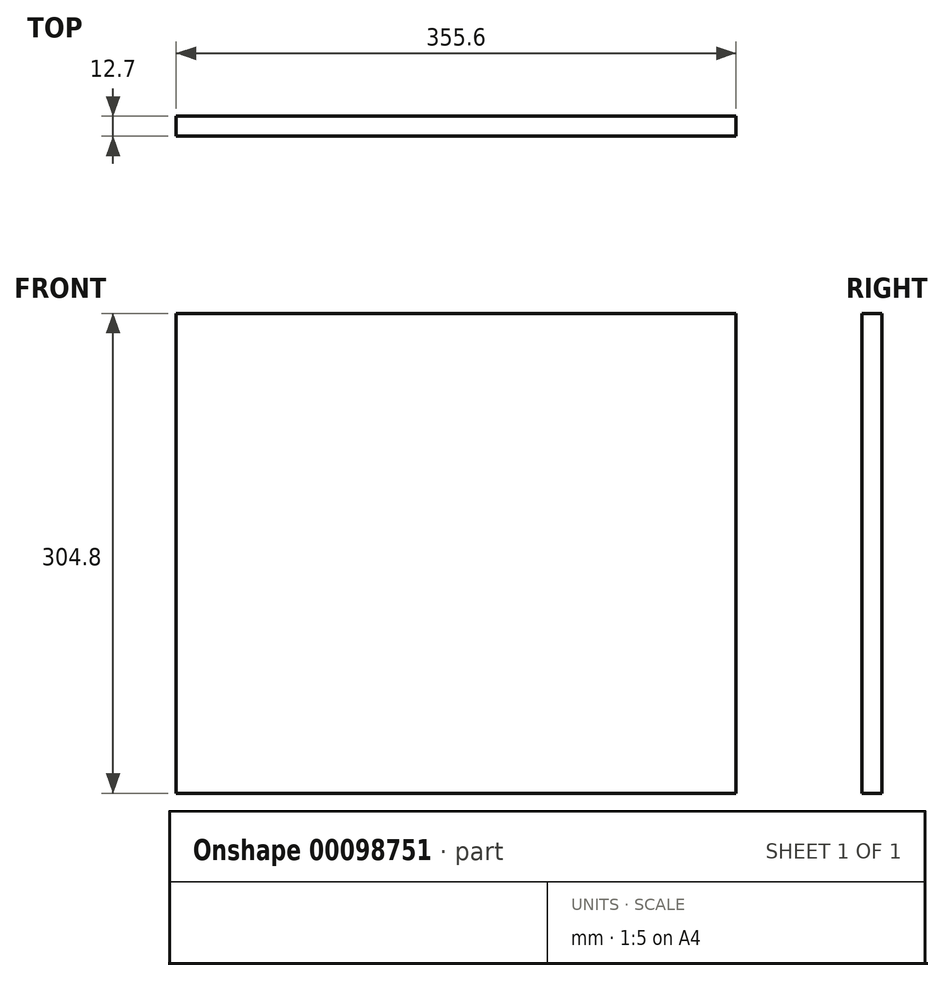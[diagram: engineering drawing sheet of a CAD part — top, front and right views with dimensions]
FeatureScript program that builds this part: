
annotation { "Feature Type Name" : "Feature", "Feature Type Description" : "" }
export const myFeature = defineFeature(function(context is Context, id is Id, definition is map)
    precondition{}
    {
        {
            var Q0;
            Q0=qCreatedBy(makeId("Front.planeOp"),FACE);
            var sketch = newSketch(context, id + "F0", { "sketchPlane" : qUnion([Q0])});
            skLineSegment(sketch, "E0.bottom", {"start": v(0, 0) * mm, "end": v(355.6, 0) * mm});
            skLineSegment(sketch, "E0.top", {"start": v(0, 304.8) * mm, "end": v(355.6, 304.8) * mm});
            skLineSegment(sketch, "E0.left", {"start": v(0, 0) * mm, "end": v(0, 304.8) * mm});
            skLineSegment(sketch, "E0.right", {"start": v(355.6, 0) * mm, "end": v(355.6, 304.8) * mm});
            skSolve(sketch);
        }
        {
            var Q0;
            Q0=makeQuery(id+"F0.imprint","IMPRINT",FACE,{"disambiguationData":[TD([[makeQuery(id+"F0.imprint","IMPRINT",EDGE,{"derivedFrom":sQuery(id+"F0.wireOp",EDGE,"E0.bottom")}),1.0]])]});
            extrude(context, id + "F1", {"entities" : qUnion([Q0]), "depth" : 12.7 * mm});
        }
    });
